# Revit family: Saltwater Chlorinator - Cell
name_source: partatom
category: Mechanical Equipment
units: mm (PartAtom-declared; Revit-internal decimal feet)

## family parameters
Always vertical = Yes
Cut with Voids When Loaded = No
OmniClass Number = 23.65.50.11.11.27
OmniClass Title = Chlorinators
Part Type = Normal
Room Calculation Point = No
Round Connector Dimension = Use Radius
Shared = No
Work Plane-Based = No

## types (4) — shared parameters
Assembly Code = D2090400
Description = Jandy Commercial Saltwater Chlorinator
Fluidra_Description = Jandy Commercial Saltwater Chlorinator
Fluidra_Manufacturer = Fluidra
Fluidra_Max_Flow_Rate = 150 GPM
Fluidra_Max_Working_Pressure = 50.00 psi
Fluidra_Salt_Level = 3000-5000 ppm
Fluidra_Union_Size = 2" - 2.5"
Manufacturer = Fluidra
URL = https://www.jandy.com

## per-type parameters (varying)
| type | Fluidra_#_Titanium_Plates | Fluidra_Chlorine_Output | Fluidra_DC_Output_(V/A) | Fluidra_Min_Flow_Rate | Fluidra_Weight | Large Electrode Connector | Small Electrode Connector |
| JSWC40 | 6 | 3.5 lbs/day | 20V / 15A | 65 GPM | 230.00 lb | No | Yes |
| JSWC80 | 11 | 7.0 lbs/day | 20V / 30A | 88 GPM | 280.00 lb | Yes | No |
| JSWC53 | 7 | 4.7 lbs/day | 24V / 16.7A | 65 GPM | 230.00 lb | No | Yes |
| JSWC100 | 13 | 8.7 lbs/day | 24V / 31.3A | 88 GPM | 280.00 lb | Yes | No |

note: column(s) folded — value = type name in every type: Fluidra_Model, Model

## geometry (parser evidence)
native form markers: Sweep x8
no freeform markers — native parametric forms only
